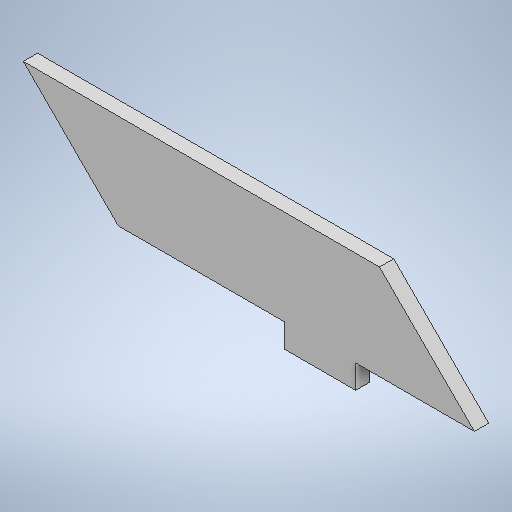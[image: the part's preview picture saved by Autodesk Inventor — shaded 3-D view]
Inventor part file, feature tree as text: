
AUTODESK INVENTOR PART (.ipt)
format: ipt  version: 2025.1 (Build 291241020, 241B)  size: 241,664 bytes
history: native  units: mm
features: extrude x1, sketch x1
ambient origin geometry x8: Origin, YZ Plane, XZ Plane, XY Plane, X Axis, Y Axis, Z Axis, Center Point
bodies: Solid1 (feature_tree)
feature tree (2):
  extrude  "Extrusion1"  Depth=15.0mm
  sketch  "Sketch1"  dims[d0=75.0mm d3=15.0mm d4=5.0mm d5=35.0mm d6=3.0mm d7=0.0mm d19=20.0mm d20=20.0mm]
